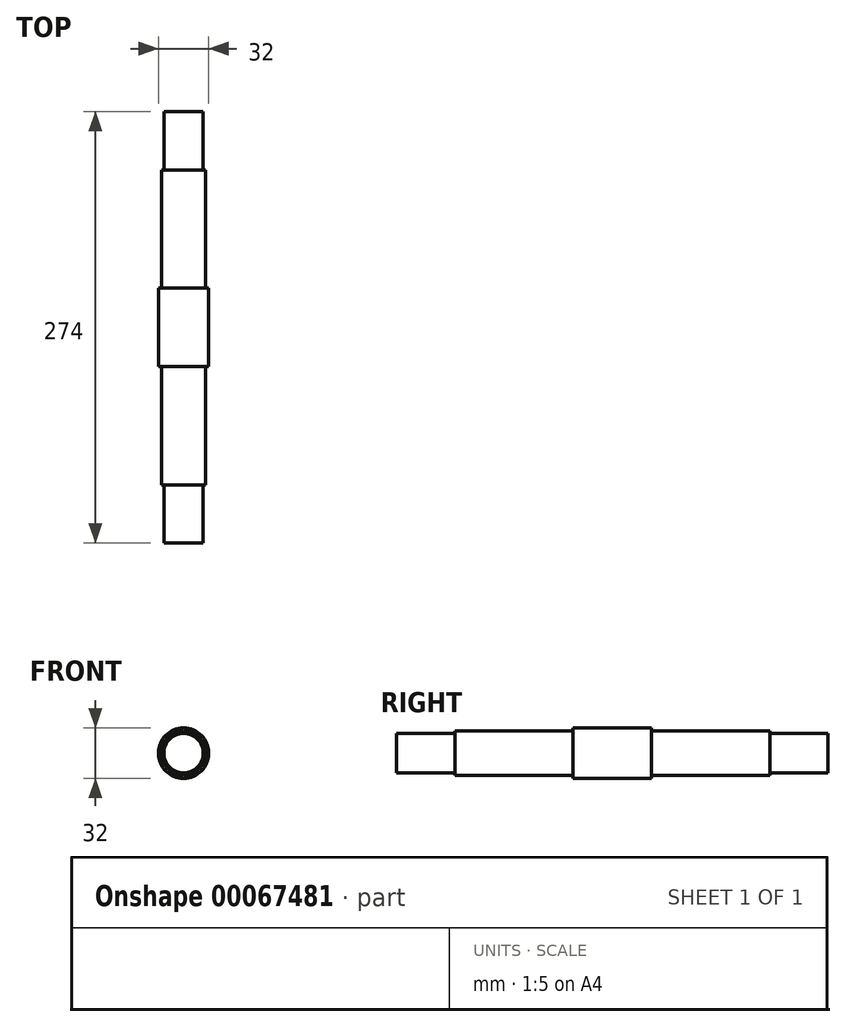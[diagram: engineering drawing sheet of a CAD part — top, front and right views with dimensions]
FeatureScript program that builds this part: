
annotation { "Feature Type Name" : "Feature", "Feature Type Description" : "" }
export const myFeature = defineFeature(function(context is Context, id is Id, definition is map)
    precondition{}
    {
        {
            var Q0;
            Q0=qCreatedBy(makeId("Front.planeOp"),FACE);
            var sketch = newSketch(context, id + "F0", { "sketchPlane" : qUnion([Q0])});
            skCircle(sketch, "E0", {"center": v(0, 0) * mm, "radius": 14 * mm});
            skCircle(sketch, "E1", {"center": v(0, 0) * mm, "radius": 16 * mm});
            skCircle(sketch, "E2", {"center": v(0, 0) * mm, "radius": 12.5 * mm});
            skSolve(sketch);
        }
        {
            var Q0;
            Q0=makeQuery(id+"F0.imprint","IMPRINT",FACE,{"disambiguationData":[TD([[makeQuery(id+"F0.imprint","IMPRINT",EDGE,{"derivedFrom":sQuery(id+"F0.wireOp",EDGE,"E2")}),1.0]])]});
            extrude(context, id + "F1", {"entities" : qUnion([Q0]), "endBound" : BoundingType.SYMMETRIC, "depth" : 274 * mm});
        }
        {
            var Q0;
            Q0=makeQuery(id+"F0.imprint","IMPRINT",FACE,{"disambiguationData":[TD([[makeQuery(id+"F0.imprint","IMPRINT",EDGE,{"derivedFrom":sQuery(id+"F0.wireOp",EDGE,"E0")}),1.0]])]});
            extrude(context, id + "F2", {"entities" : qUnion([Q0]), "operationType" : NewBodyOperationType.ADD, "endBound" : BoundingType.SYMMETRIC, "depth" : 200 * mm});
        }
        {
            var Q0;
            Q0=makeQuery(id+"F0.imprint","IMPRINT",FACE,{"disambiguationData":[TD([[makeQuery(id+"F0.imprint","IMPRINT",EDGE,{"derivedFrom":sQuery(id+"F0.wireOp",EDGE,"E0")}),-1.0]])]});
            extrude(context, id + "F3", {"entities" : qUnion([Q0]), "operationType" : NewBodyOperationType.ADD, "endBound" : BoundingType.SYMMETRIC, "depth" : 50 * mm});
        }
    });
